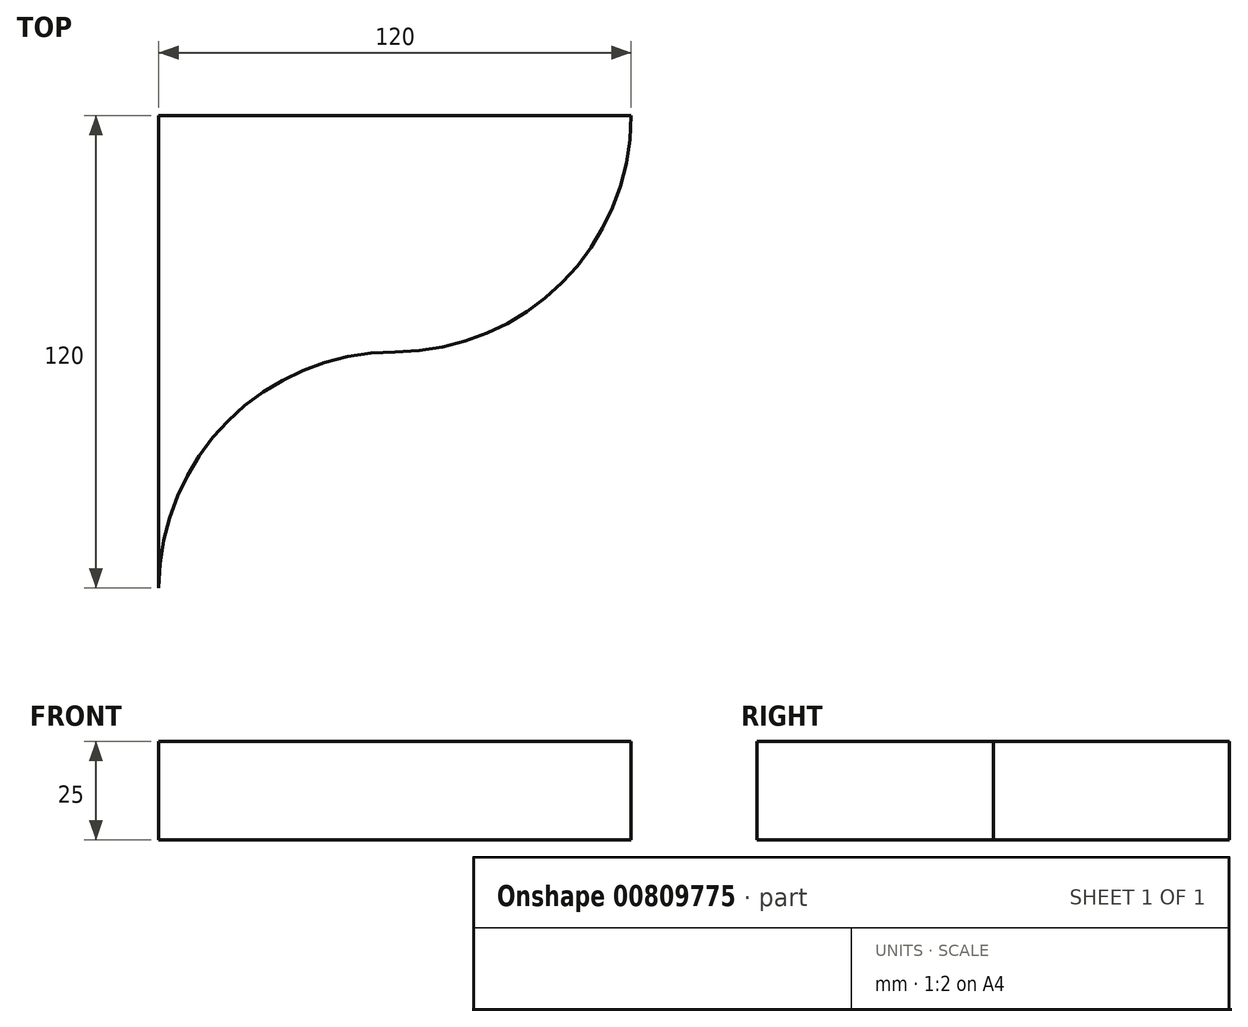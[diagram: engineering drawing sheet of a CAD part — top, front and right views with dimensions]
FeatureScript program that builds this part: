
annotation { "Feature Type Name" : "Feature", "Feature Type Description" : "" }
export const myFeature = defineFeature(function(context is Context, id is Id, definition is map)
    precondition{}
    {
        {
            var Q0;
            Q0=qCreatedBy(makeId("Top.planeOp"),FACE);
            var sketch = newSketch(context, id + "F0", { "sketchPlane" : qUnion([Q0])});
            skLineSegment(sketch, "E0.bottom", {"start": v(-60, 0) * mm, "end": v(-60, 0) * mm});
            skLineSegment(sketch, "E0.top", {"start": v(0, 120) * mm, "end": v(-60, 120) * mm});
            skLineSegment(sketch, "E0.left", {"start": v(0, 60) * mm, "end": v(0, 120) * mm});
            skLineSegment(sketch, "E0.right", {"start": v(-60, 0) * mm, "end": v(-60, 120) * mm});
            skArc(sketch, "E1", {"start": v(0, 60) * mm, "mid": v(-42.43, 42.43) * mm, "end": v(-60, 0) * mm});
            skArc(sketch, "E2", {"start": v(0, 60) * mm, "mid": v(42.43, 77.57) * mm, "end": v(60, 120) * mm});
            skLineSegment(sketch, "E3", {"start": v(0, 120) * mm, "end": v(60, 120) * mm});
            skSolve(sketch);
        }
        {
            var Q0;
            Q0=makeQuery(id+"F0.imprint","IMPRINT",FACE,{"disambiguationData":[TD([[makeQuery(id+"F0.imprint","IMPRINT",EDGE,{"derivedFrom":sQuery(id+"F0.wireOp",EDGE,"E0.left")}),-1.0]])]});
            var Q1;
            Q1=makeQuery(id+"F0.imprint","IMPRINT",FACE,{"disambiguationData":[TD([[makeQuery(id+"F0.imprint","IMPRINT",EDGE,{"derivedFrom":sQuery(id+"F0.wireOp",EDGE,"E0.top")}),1.0]])]});
            extrude(context, id + "F1", {"entities" : qUnion([Q0, Q1]), "depth" : 25 * mm, "offsetDistance" : 25 * mm});
        }
    });
